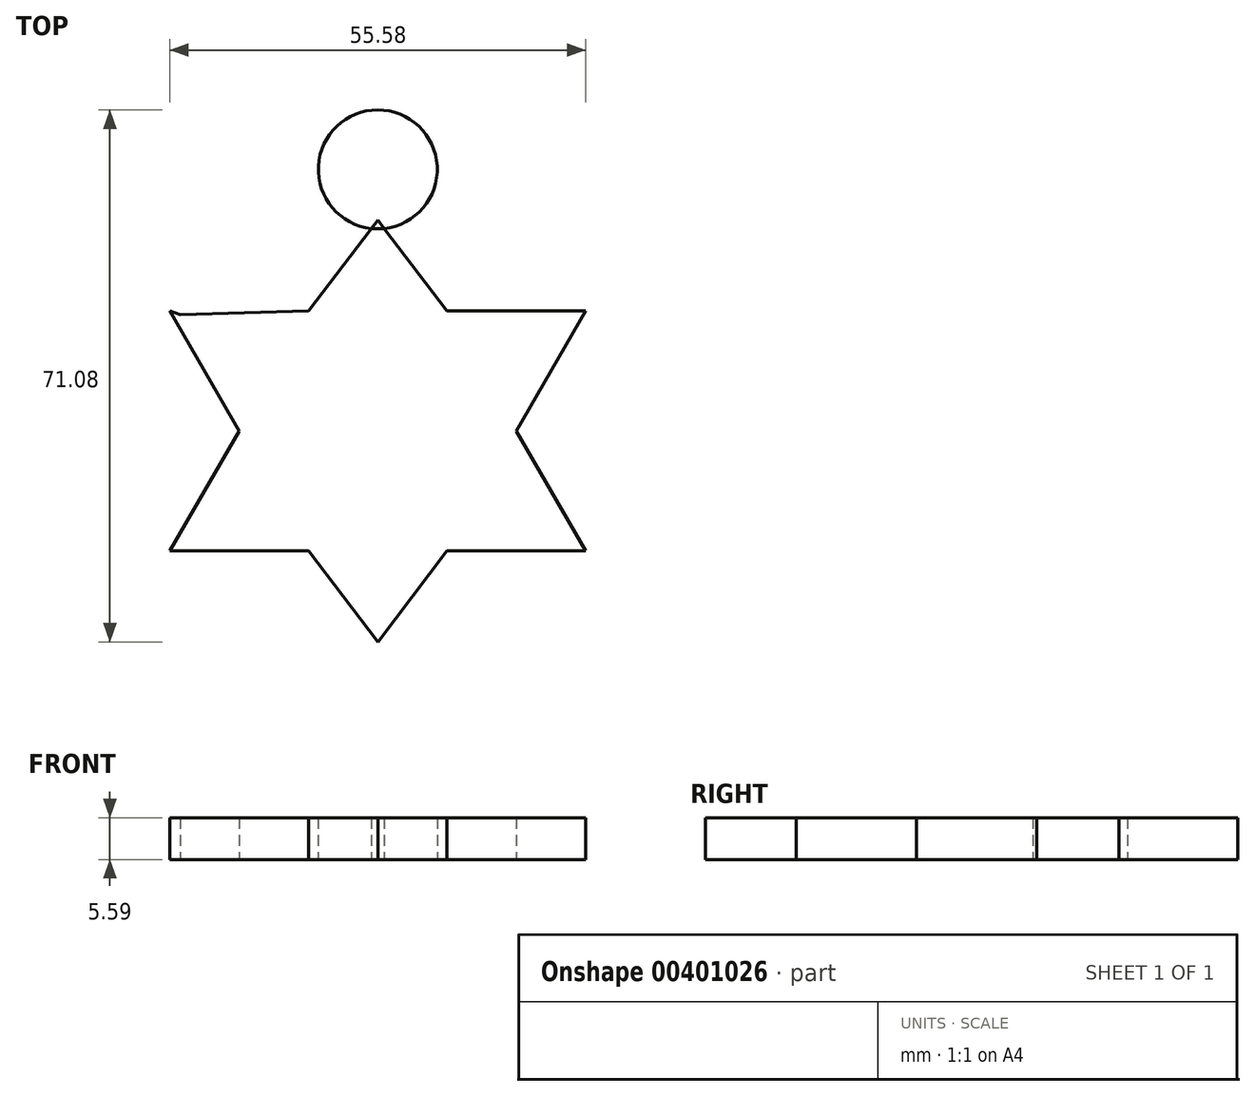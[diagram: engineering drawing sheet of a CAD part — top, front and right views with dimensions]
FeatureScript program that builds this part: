
annotation { "Feature Type Name" : "Feature", "Feature Type Description" : "" }
export const myFeature = defineFeature(function(context is Context, id is Id, definition is map)
    precondition{}
    {
        {
            var Q0;
            Q0=qCreatedBy(makeId("Top.planeOp"),FACE);
            var sketch = newSketch(context, id + "F0", { "sketchPlane" : qUnion([Q0])});
            skCircle(sketch, "E0.cCircle", {"center": v(0, 0) * mm, "radius": 16.05 * mm, "construction": true});
            skLineSegment(sketch, "E0.0", {"start": v(-9.26, 16.05) * mm, "end": v(9.26, 16.05) * mm});
            skLineSegment(sketch, "E0.1", {"start": v(9.26, 16.05) * mm, "end": v(18.53, 0) * mm});
            skLineSegment(sketch, "E0.2", {"start": v(18.53, 0) * mm, "end": v(9.26, -16.05) * mm});
            skLineSegment(sketch, "E0.3", {"start": v(9.26, -16.05) * mm, "end": v(-9.26, -16.05) * mm});
            skLineSegment(sketch, "E0.4", {"start": v(-9.26, -16.05) * mm, "end": v(-18.53, 0) * mm});
            skLineSegment(sketch, "E0.5", {"start": v(-18.53, 0) * mm, "end": v(-9.26, 16.05) * mm});
            skPoint(sketch, "E0.0.midPoint", {"position": v(0, 16.05) * mm});
            skLineSegment(sketch, "E1", {"start": v(-9.26, 16.05) * mm, "end": v(0, 28.18) * mm});
            skLineSegment(sketch, "E2", {"start": v(0, 28.18) * mm, "end": v(9.26, 16.05) * mm});
            skLineSegment(sketch, "E3", {"start": v(-9.26, -16.05) * mm, "end": v(0, -28.18) * mm});
            skLineSegment(sketch, "E4", {"start": v(0, -28.18) * mm, "end": v(9.26, -16.05) * mm});
            skLineSegment(sketch, "E5", {"start": v(9.26, 16.05) * mm, "end": v(27.8, 16.05) * mm});
            skLineSegment(sketch, "E6", {"start": v(27.8, 16.05) * mm, "end": v(18.53, 0) * mm});
            skLineSegment(sketch, "E7", {"start": v(9.26, -16.05) * mm, "end": v(27.8, -16.05) * mm});
            skLineSegment(sketch, "E8", {"start": v(27.8, -16.05) * mm, "end": v(18.53, 0) * mm});
            skLineSegment(sketch, "E9", {"start": v(-18.53, 0) * mm, "end": v(-27.8, -16.05) * mm});
            skLineSegment(sketch, "E10", {"start": v(-9.26, -16.05) * mm, "end": v(-27.8, -16.05) * mm});
            skLineSegment(sketch, "E11", {"start": v(-18.53, 0) * mm, "end": v(-27.8, 16.05) * mm});
            skLineSegment(sketch, "E12", {"start": v(-27.8, 16.05) * mm, "end": v(-26.4, 15.57) * mm});
            skLineSegment(sketch, "E13", {"start": v(-9.26, 16.05) * mm, "end": v(-26.4, 15.57) * mm});
            skCircle(sketch, "E14", {"center": v(0, 34.96) * mm, "radius": 7.94 * mm});
            skSolve(sketch);
        }
        {
            var Q0;
            Q0=makeQuery(id+"F0.imprint","IMPRINT",FACE,{"disambiguationData":[TD([[makeQuery(id+"F0.imprint","IMPRINT",EDGE,{"derivedFrom":sQuery(id+"F0.wireOp",EDGE,"E0.0")}),-1.0]])]});
            var Q1;
            {var subQ0=sQuery(id+"F0.wireOp",EDGE,"E0.0");Q1=makeQuery(id+"F0.imprint","IMPRINT",FACE,{"disambiguationData":[TD([[makeQuery(id+"F0.imprint","IMPRINT",EDGE,{"derivedFrom":subQ0}),1.0]])]});}
            var Q2;
            Q2=makeQuery(id+"F0.imprint","IMPRINT",FACE,{"disambiguationData":[TD([[makeQuery(id+"F0.imprint","IMPRINT",EDGE,{"derivedFrom":sQuery(id+"F0.wireOp",EDGE,"E0.5")}),1.0]])]});
            var Q3;
            Q3=makeQuery(id+"F0.imprint","IMPRINT",FACE,{"disambiguationData":[TD([[makeQuery(id+"F0.imprint","IMPRINT",EDGE,{"derivedFrom":sQuery(id+"F0.wireOp",EDGE,"E0.4")}),1.0]])]});
            var Q4;
            Q4=makeQuery(id+"F0.imprint","IMPRINT",FACE,{"disambiguationData":[TD([[makeQuery(id+"F0.imprint","IMPRINT",EDGE,{"derivedFrom":sQuery(id+"F0.wireOp",EDGE,"E0.3")}),1.0]])]});
            var Q5;
            Q5=makeQuery(id+"F0.imprint","IMPRINT",FACE,{"disambiguationData":[TD([[makeQuery(id+"F0.imprint","IMPRINT",EDGE,{"derivedFrom":sQuery(id+"F0.wireOp",EDGE,"E0.2")}),1.0]])]});
            var Q6;
            Q6=makeQuery(id+"F0.imprint","IMPRINT",FACE,{"disambiguationData":[TD([[makeQuery(id+"F0.imprint","IMPRINT",EDGE,{"derivedFrom":sQuery(id+"F0.wireOp",EDGE,"E0.1")}),1.0]])]});
            var Q7;
            {var subQ0=sQuery(id+"F0.wireOp",EDGE,"E2");var subQ1=sQuery(id+"F0.wireOp",EDGE,"E1");var subQ2=makeQuery(id+"F0.imprint","INTERSECT",VERTEX,{"derivedFrom":[subQ1,subQ0]});Q7=makeQuery(id+"F0.imprint","IMPRINT",FACE,{"disambiguationData":[TD([[makeQuery(id+"F0.imprint","IMPRINT",EDGE,{"disambiguationData":[TD([[subQ2,1.0]])],"derivedFrom":subQ1}),1.0]])]});}
            extrude(context, id + "F1", {"entities" : qUnion([Q0, Q1, Q2, Q3, Q4, Q5, Q6, Q7]), "depth" : 5.6 * mm});
        }
    });
